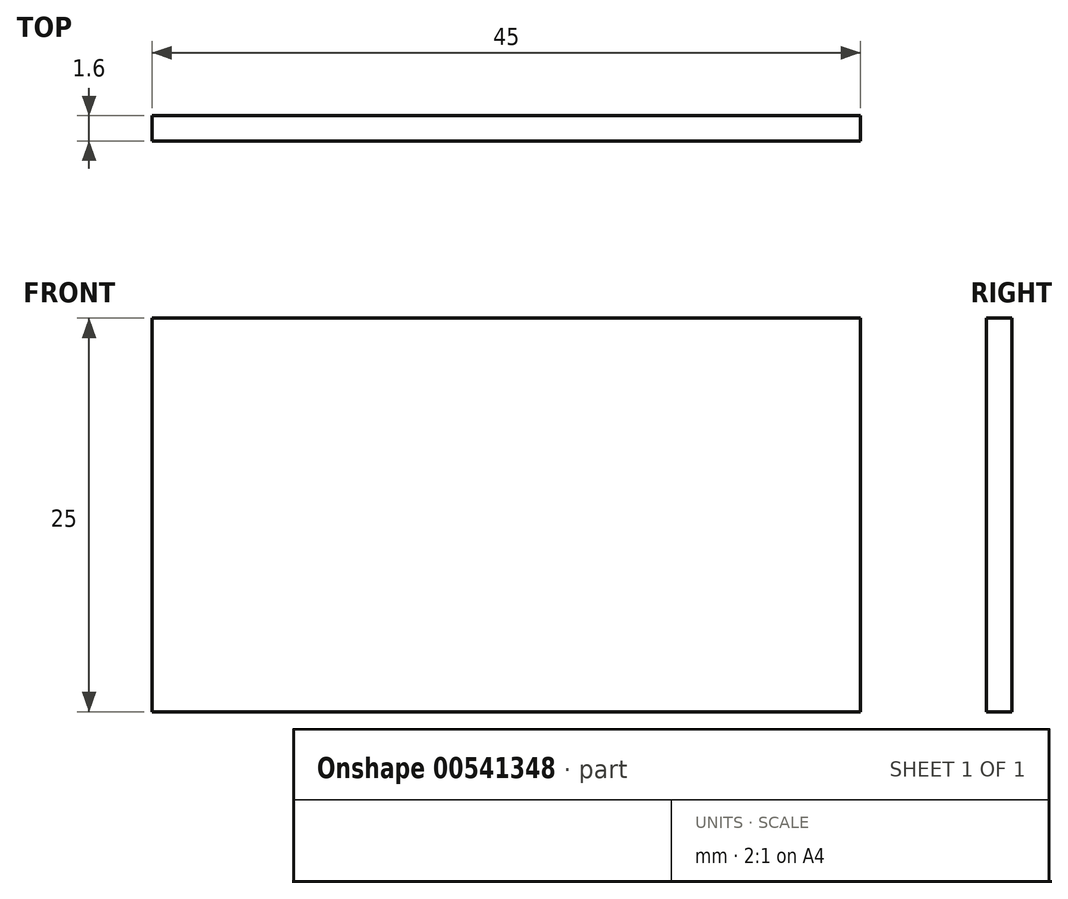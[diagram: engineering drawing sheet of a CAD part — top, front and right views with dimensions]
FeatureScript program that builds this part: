
annotation { "Feature Type Name" : "Feature", "Feature Type Description" : "" }
export const myFeature = defineFeature(function(context is Context, id is Id, definition is map)
    precondition{}
    {
        {
            var Q0;
            Q0=qCreatedBy(makeId("Front.planeOp"),FACE);
            var sketch = newSketch(context, id + "F0", { "sketchPlane" : qUnion([Q0])});
            skLineSegment(sketch, "E0.bottom", {"start": v(22.5, -12.5) * mm, "end": v(-22.5, -12.5) * mm});
            skLineSegment(sketch, "E0.top", {"start": v(22.5, 12.5) * mm, "end": v(-22.5, 12.5) * mm});
            skLineSegment(sketch, "E0.left", {"start": v(22.5, -12.5) * mm, "end": v(22.5, 12.5) * mm});
            skLineSegment(sketch, "E0.right", {"start": v(-22.5, -12.5) * mm, "end": v(-22.5, 12.5) * mm});
            skPoint(sketch, "E0.middle", {"position": v(0, 0) * mm});
            skSolve(sketch);
        }
        {
            var Q0;
            Q0 = qSketchRegion(id + "F0", true);
            extrude(context, id + "F1", {"entities" : qUnion([Q0]), "depth" : 1.6 * mm, "offsetDistance" : 25.4 * mm});
        }
    });
